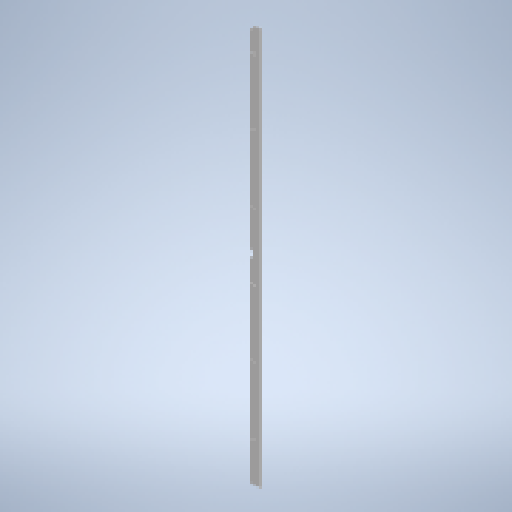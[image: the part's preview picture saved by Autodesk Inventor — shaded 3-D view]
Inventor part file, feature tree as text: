
AUTODESK INVENTOR PART (.ipt)
format: ipt  version: 2025 (Build 290162010, 162A)  size: 384,512 bytes
history: native  units: mm
features: other x4, sketch x4, projected_geometry x3, extrude x2, pattern_linear x2, sheet_metal_op x1
ambient origin geometry x8: Origin, YZ Plane, XZ Plane, XY Plane, X Axis, Y Axis, Z Axis, Center Point
bodies: Body1 (feature_tree)
feature tree (16):
  sheet_metal_op  "Face2"
  other  "Mark1"
  extrude  "Extrusion2"  Depth=2980.0mm
  pattern_linear  "Rectangular Pattern1"  Spacing1=0.0mm  [1 undecoded]
  extrude  "Extrusion3"  Depth=10.0mm
  pattern_linear  "Rectangular Pattern2"  Count1=5  [1 undecoded]
  other  "Corner Chamfer1"
  sketch  "Sketch6"  dims[d26=80.45761mm d27=2980.0mm]
  other  "Plate4"
  sketch  "Sketch7"  dims[d28=3.0mm]
  projected_geometry  "Projected Loop1"
  sketch  "Sketch8"  dims[d29=41.228805mm]
  projected_geometry  "Projected Loop2"
  sketch  "Sketch9"  dims[d30=3.2mm d32=0.0mm d33=0.0mm d34=60.0mm d36=500.0mm d37=50.0mm d38=1490.0mm d39=0.0mm d40=0.0mm d41=20.0mm d43=1480.0mm d44=200.0mm d45=15.0mm d47=10.0mm d48=6.0mm d49=6.0mm d50=45.0deg d51=182.0mm]
  projected_geometry  "Projected Loop3"
  other  "Definition1"
note: 2 required parameter values undecoded (feature->parameter linkage not recoverable at this tier; creation-order binding heuristic only, values carry confidence <= 0.55)
